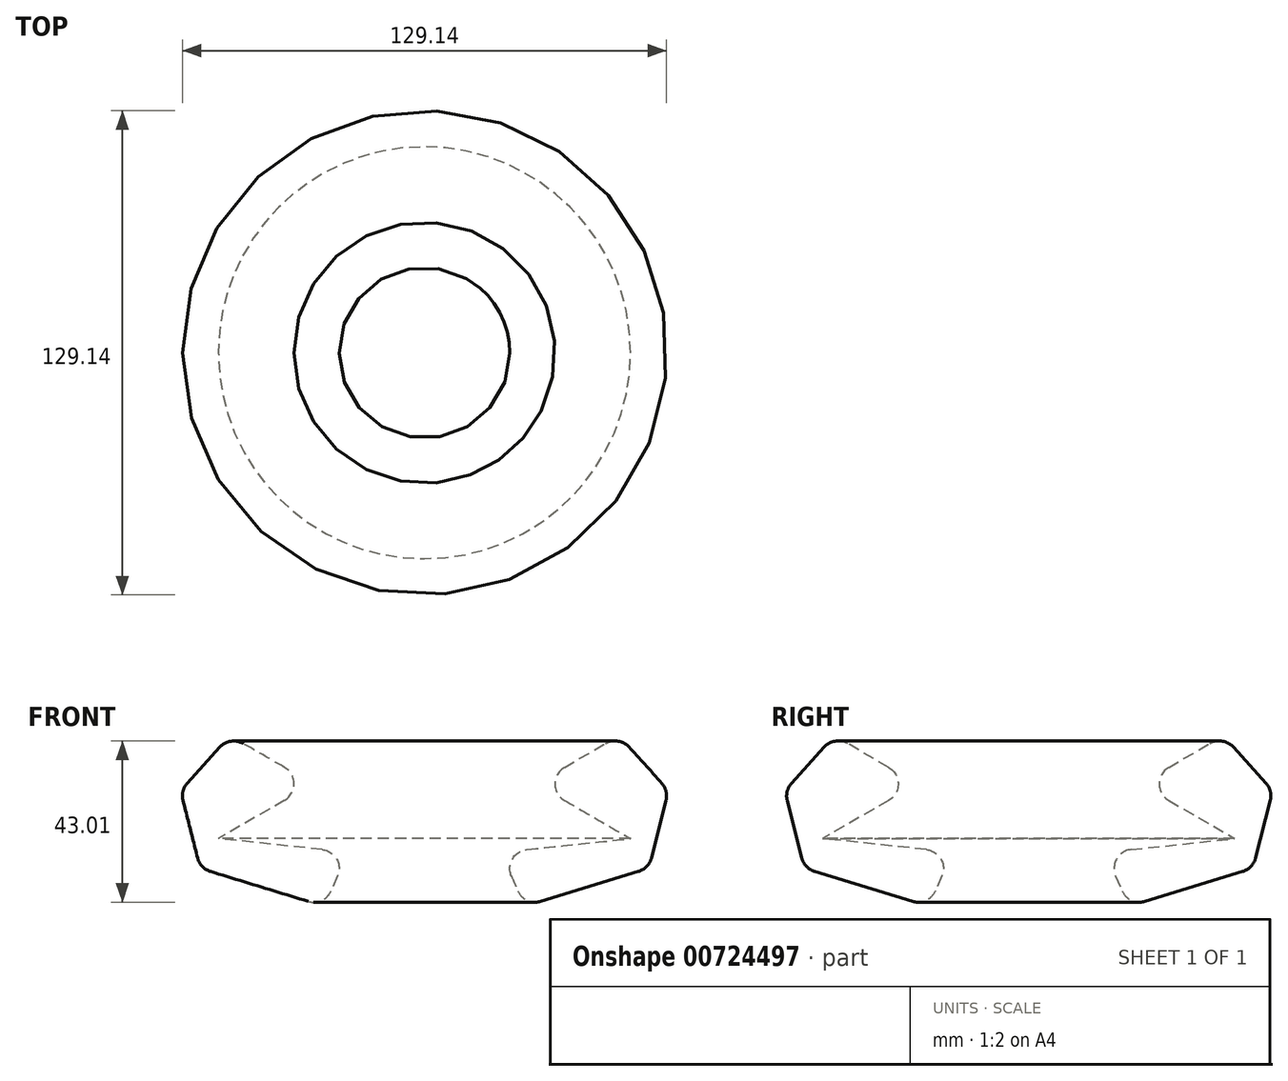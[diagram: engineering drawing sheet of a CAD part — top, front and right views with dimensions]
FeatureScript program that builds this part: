
annotation { "Feature Type Name" : "Feature", "Feature Type Description" : "" }
export const myFeature = defineFeature(function(context is Context, id is Id, definition is map)
    precondition{}
    {
        {
            var Q0;
            Q0=qCreatedBy(makeId("Front.planeOp"),FACE);
            var sketch = newSketch(context, id + "F0", { "sketchPlane" : qUnion([Q0])});
            skLineSegment(sketch, "E0", {"start": v(-65.08, -20.4) * mm, "end": v(-59.8, -41.12) * mm});
            skLineSegment(sketch, "E1", {"start": v(-59.8, -41.12) * mm, "end": v(-26.7, -51.28) * mm});
            skLineSegment(sketch, "E2", {"start": v(-26.7, -51.28) * mm, "end": v(-20.4, -36.86) * mm});
            skLineSegment(sketch, "E3", {"start": v(-20.4, -36.86) * mm, "end": v(-54.93, -33.2) * mm});
            skLineSegment(sketch, "E4", {"start": v(-54.93, -33.2) * mm, "end": v(-29.75, -18.58) * mm});
            skLineSegment(sketch, "E5", {"start": v(-29.75, -18.58) * mm, "end": v(-51.88, -5.79) * mm});
            skLineSegment(sketch, "E6", {"start": v(-51.88, -5.79) * mm, "end": v(-65.08, -20.4) * mm});
            skSolve(sketch);
        }
        {
            var Q0;
            Q0=qCreatedBy(makeId("Front.planeOp"),FACE);
            var sketch = newSketch(context, id + "F1", { "sketchPlane" : qUnion([Q0])});
            skLineSegment(sketch, "E7", {"start": v(0, 25.08) * mm, "end": v(0, -29.75) * mm});
            skSolve(sketch);
        }
        {
            var Q0;
            Q0=makeQuery(id+"F0.imprint","IMPRINT",FACE,{"disambiguationData":[TD([[makeQuery(id+"F0.imprint","IMPRINT",EDGE,{"derivedFrom":sQuery(id+"F0.wireOp",EDGE,"E0")}),1.0]])]});
            var Q1;
            Q1=sQuery(id+"F1.wireOp",EDGE,"E7");
            revolve(context, id + "F2", {"surfaceOperationType" : NewSurfaceOperationType.NEW, "entities" : qUnion([Q0]), "axis" : qUnion([Q1]), "revolveType" : RevolveType.FULL});
        }
        {
            var Q0;
            Q0=makeQuery(id+"F2.opRevolve","SWEPT_EDGE",EDGE,{"disambiguationData":[OSD([sQuery(id+"F0.wireOp",EDGE,"E5"),sQuery(id+"F0.wireOp",EDGE,"E6")])]});
            fillet(context, id + "F3", {"entities" : qUnion([Q0]), "radius" : 5.08 * mm, "tangentPropagation" : true, "allowEdgeOverflow" : false});
        }
        {
            var Q0;
            Q0=makeQuery(id+"F2.opRevolve","SWEPT_EDGE",EDGE,{"disambiguationData":[OSD([sQuery(id+"F0.wireOp",EDGE,"E0"),sQuery(id+"F0.wireOp",EDGE,"E6")])]});
            fillet(context, id + "F4", {"entities" : qUnion([Q0]), "radius" : 5.08 * mm, "tangentPropagation" : true, "allowEdgeOverflow" : false});
        }
        {
            var Q0;
            Q0=makeQuery(id+"F2.opRevolve","SWEPT_EDGE",EDGE,{"disambiguationData":[OSD([sQuery(id+"F0.wireOp",EDGE,"E0"),sQuery(id+"F0.wireOp",EDGE,"E1")])]});
            fillet(context, id + "F5", {"entities" : qUnion([Q0]), "radius" : 5.08 * mm, "tangentPropagation" : true, "allowEdgeOverflow" : false});
        }
        {
            var Q0;
            Q0=makeQuery(id+"F2.opRevolve","SWEPT_EDGE",EDGE,{"disambiguationData":[OSD([sQuery(id+"F0.wireOp",EDGE,"E1"),sQuery(id+"F0.wireOp",EDGE,"E2")])]});
            fillet(context, id + "F6", {"entities" : qUnion([Q0]), "radius" : 5.08 * mm, "tangentPropagation" : true, "allowEdgeOverflow" : false});
        }
        {
            var Q0;
            Q0=makeQuery(id+"F2.opRevolve","SWEPT_EDGE",EDGE,{"disambiguationData":[OSD([sQuery(id+"F0.wireOp",EDGE,"E4"),sQuery(id+"F0.wireOp",EDGE,"E5")])]});
            fillet(context, id + "F7", {"entities" : qUnion([Q0]), "radius" : 5.08 * mm, "tangentPropagation" : true, "allowEdgeOverflow" : false});
        }
        {
            var Q0;
            Q0=makeQuery(id+"F2.opRevolve","SWEPT_EDGE",EDGE,{"disambiguationData":[OSD([sQuery(id+"F0.wireOp",EDGE,"E2"),sQuery(id+"F0.wireOp",EDGE,"E3")])]});
            fillet(context, id + "F8", {"entities" : qUnion([Q0]), "radius" : 5.08 * mm, "tangentPropagation" : true, "allowEdgeOverflow" : false});
        }
    });
